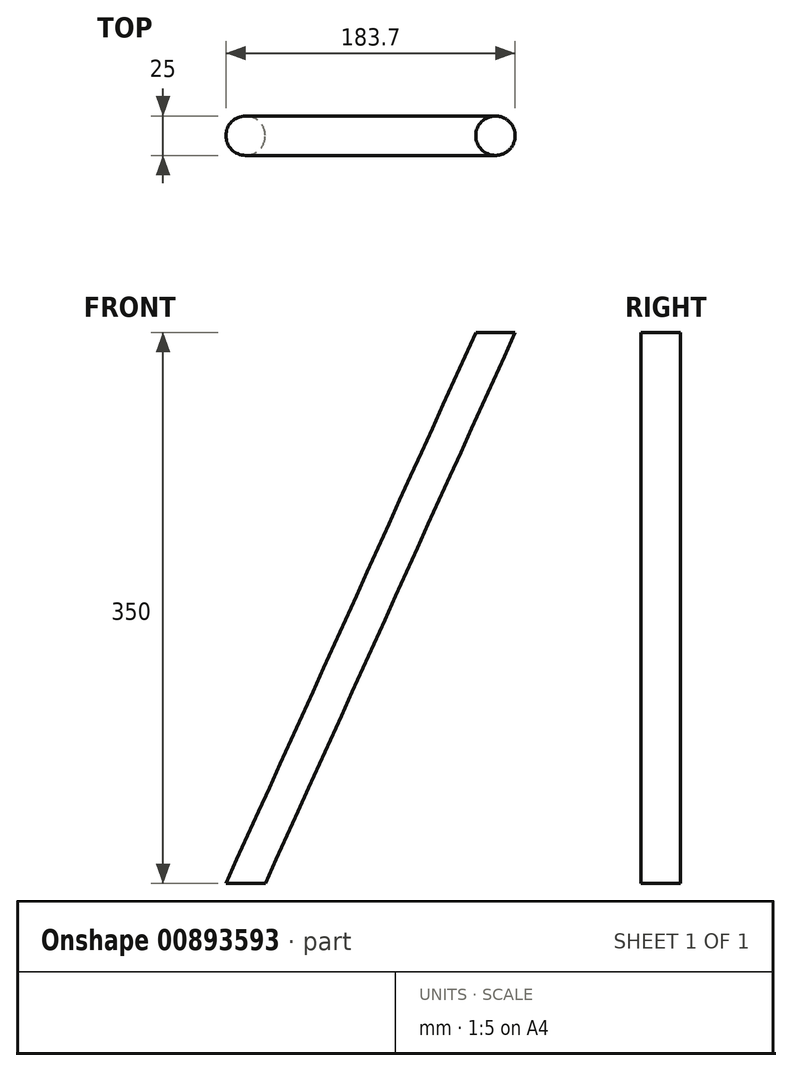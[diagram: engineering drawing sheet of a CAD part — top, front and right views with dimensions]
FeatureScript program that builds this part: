
annotation { "Feature Type Name" : "Feature", "Feature Type Description" : "" }
export const myFeature = defineFeature(function(context is Context, id is Id, definition is map)
    precondition{}
    {
        {
            var Q0;
            Q0=qCreatedBy(makeId("Front.planeOp"),FACE);
            var sketch = newSketch(context, id + "F0", { "sketchPlane" : qUnion([Q0])});
            skLineSegment(sketch, "E0", {"start": v(0, 0) * mm, "end": v(158.7, 350) * mm});
            skLineSegment(sketch, "E1", {"start": v(158.7, 350) * mm, "end": v(325.64, 0) * mm});
            skSolve(sketch);
        }
        {
            var Q0;
            Q0=qCreatedBy(makeId("Top.planeOp"),FACE);
            var sketch = newSketch(context, id + "F1", { "sketchPlane" : qUnion([Q0])});
            skCircle(sketch, "E2", {"center": v(0, 0) * mm, "radius": 12.5 * mm});
            skSolve(sketch);
        }
        {
            var Q0;
            Q0=makeQuery(id+"F1.imprint","IMPRINT",FACE,{"disambiguationData":[TD([[makeQuery(id+"F1.imprint","IMPRINT",EDGE,{"derivedFrom":sQuery(id+"F1.wireOp",EDGE,"E2")}),1.0]])]});
            var Q1;
            Q1=sQuery(id+"F0.wireOp",EDGE,"E0");
            sweep(context, id + "F2", {"profiles" : qUnion([Q0]), "path" : qUnion([Q1])});
        }
    });
